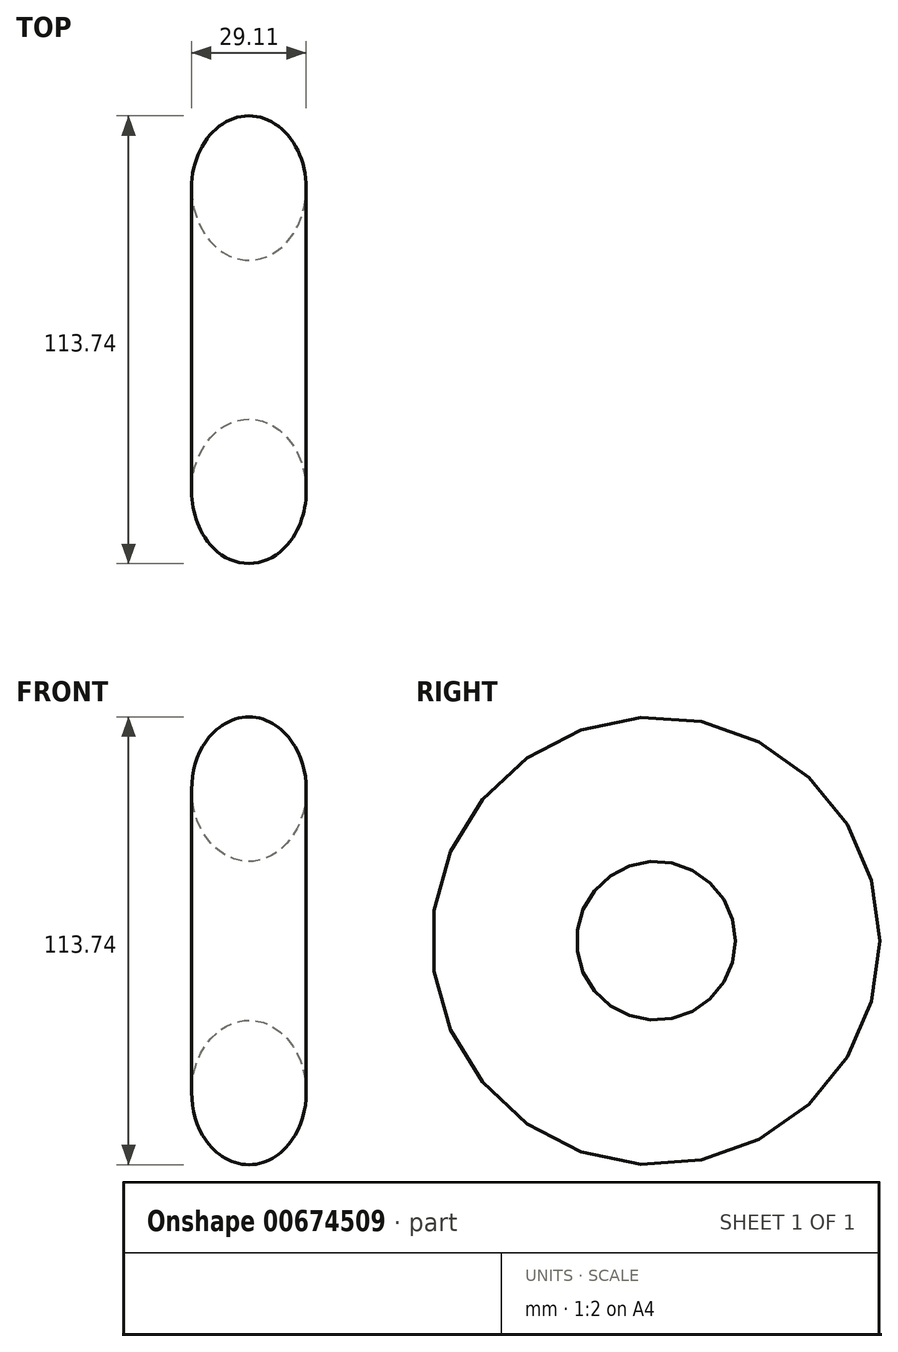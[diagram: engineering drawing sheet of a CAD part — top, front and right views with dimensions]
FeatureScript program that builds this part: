
annotation { "Feature Type Name" : "Feature", "Feature Type Description" : "" }
export const myFeature = defineFeature(function(context is Context, id is Id, definition is map)
    precondition{}
    {
        {
            var Q0;
            Q0=qCreatedBy(makeId("Top.planeOp"),FACE);
            var sketch = newSketch(context, id + "F0", { "sketchPlane" : qUnion([Q0])});
            skEllipse(sketch, "E0", {"center": v(-16.08, 38.52) * mm, "majorRadius": 18.36 * mm, "minorRadius": 14.56 * mm, "majorAxis": v(0, 1)});
            skLineSegment(sketch, "E1", {"start": v(-33.2, 0) * mm, "end": v(0, 0) * mm, "construction": true});
            skSolve(sketch);
        }
        {
            var Q0;
            Q0=sQuery(id+"F0.wireOp",EDGE,"E1");
            var Q1;
            Q1=sQuery(id+"F0.wireOp",EDGE,"E0");
            var Q2;
            Q2=sQuery(id+"F0.wireOp",EDGE,"E1");
            revolve(context, id + "F1", {"bodyType" : ToolBodyType.SURFACE, "surfaceEntities" : qUnion([Q0, Q1]), "axis" : qUnion([Q2]), "revolveType" : RevolveType.FULL});
        }
    });
